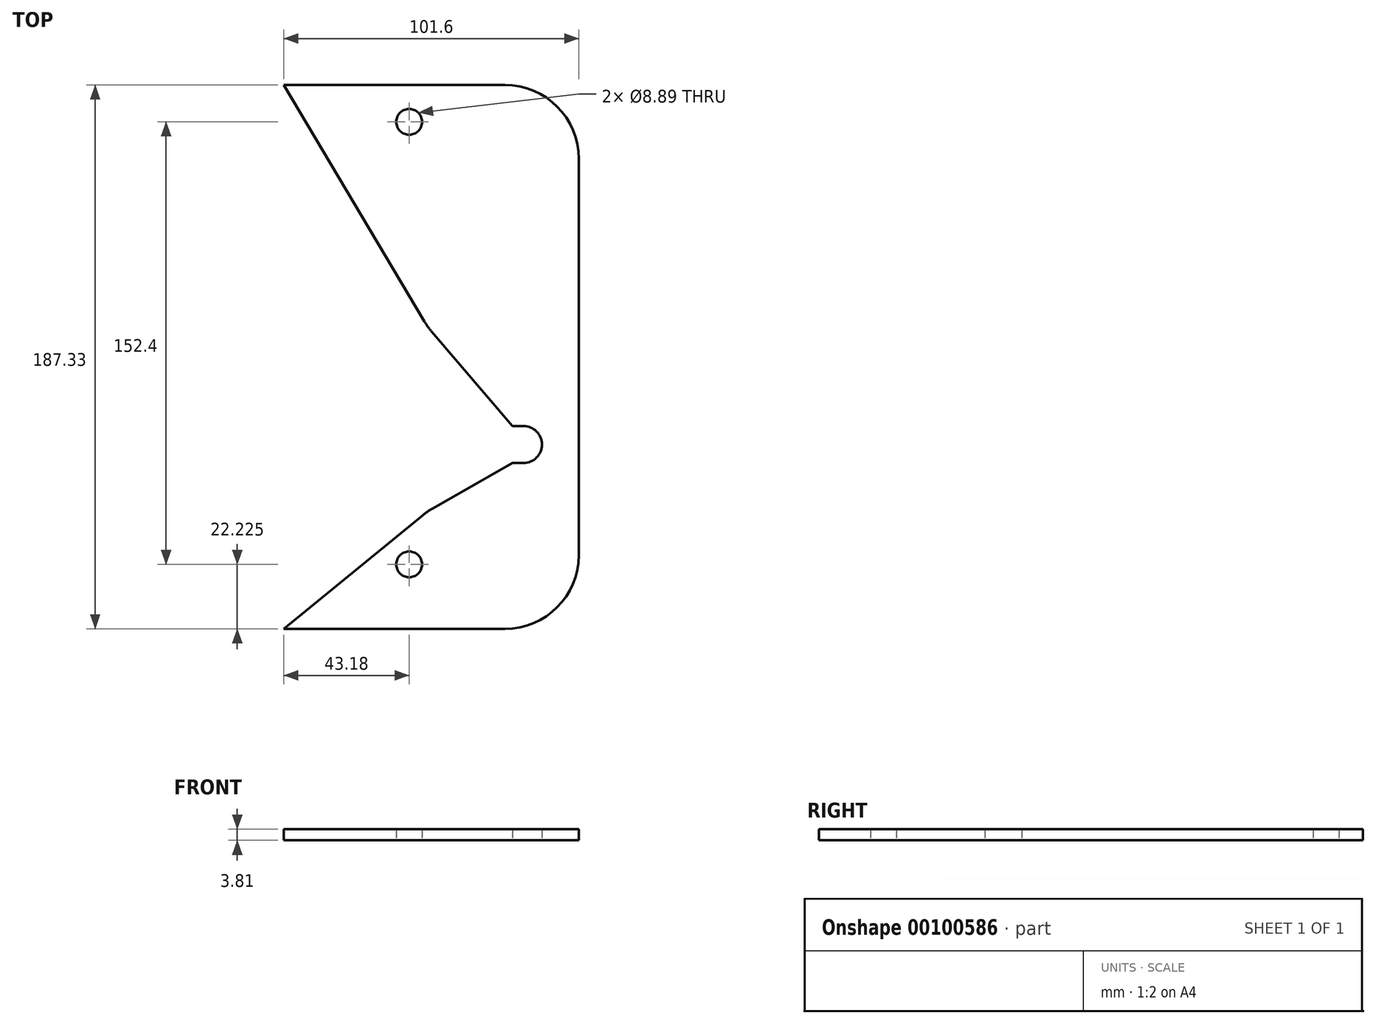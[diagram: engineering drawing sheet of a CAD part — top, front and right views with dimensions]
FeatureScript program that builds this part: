
annotation { "Feature Type Name" : "Feature", "Feature Type Description" : "" }
export const myFeature = defineFeature(function(context is Context, id is Id, definition is map)
    precondition{}
    {
        {
            var Q0;
            Q0=qCreatedBy(makeId("Top.planeOp"),FACE);
            var sketch = newSketch(context, id + "F0", { "sketchPlane" : qUnion([Q0])});
            skLineSegment(sketch, "E0.bottom", {"start": v(0, 0) * mm, "end": v(101.6, 0) * mm});
            skLineSegment(sketch, "E0.top", {"start": v(0, 187.33) * mm, "end": v(101.6, 187.33) * mm});
            skLineSegment(sketch, "E0.left", {"start": v(0, 0) * mm, "end": v(0, 187.33) * mm});
            skLineSegment(sketch, "E0.right", {"start": v(101.6, 0) * mm, "end": v(101.6, 187.33) * mm});
            skPoint(sketch, "E1.endSnap0", {"position": v(101.6, 93.66) * mm});
            skLineSegment(sketch, "E2", {"start": v(69.85, 57.15) * mm, "end": v(0, 0) * mm});
            skLineSegment(sketch, "E3", {"start": v(69.85, 69.85) * mm, "end": v(0, 187.33) * mm});
            skCircle(sketch, "E4", {"center": v(43.18, 22.23) * mm, "radius": 4.45 * mm});
            skCircle(sketch, "E5", {"center": v(43.18, 174.63) * mm, "radius": 4.45 * mm});
            skLineSegment(sketch, "E6", {"start": v(69.85, 69.85) * mm, "end": v(82.55, 69.85) * mm});
            skLineSegment(sketch, "E7", {"start": v(82.55, 69.85) * mm, "end": v(82.55, 57.15) * mm});
            skLineSegment(sketch, "E8", {"start": v(82.55, 57.15) * mm, "end": v(69.85, 57.15) * mm});
            skCircle(sketch, "E9", {"center": v(82.55, 63.5) * mm, "radius": 6.35 * mm});
            skPoint(sketch, "E10", {"position": v(88.9, 63.5) * mm});
            skLineSegment(sketch, "E11", {"start": v(78.74, 69.85) * mm, "end": v(49.53, 104.02) * mm});
            skLineSegment(sketch, "E12", {"start": v(78.74, 57.15) * mm, "end": v(49.53, 40.52) * mm});
            skSolve(sketch);
        }
        {
            var Q0;
            {var subQ5=sQuery(id+"F0.wireOp",EDGE,"E0.top");Q0=makeQuery(id+"F0.imprint","IMPRINT",FACE,{"disambiguationData":[TD([[makeQuery(id+"F0.imprint","IMPRINT",EDGE,{"derivedFrom":subQ5}),-1.0]])]});}
            var Q1;
            {var subQ6=sQuery(id+"F0.wireOp",EDGE,"E0.bottom");Q1=makeQuery(id+"F0.imprint","IMPRINT",FACE,{"disambiguationData":[TD([[makeQuery(id+"F0.imprint","IMPRINT",EDGE,{"derivedFrom":subQ6}),1.0]])]});}
            extrude(context, id + "F1", {"entities" : qUnion([Q0, Q1]), "depth" : 3.8 * mm});
        }
        {
            var Q0;
            Q0=makeQuery(id+"F1.opExtrude","SWEPT_EDGE",EDGE,{"disambiguationData":[OSD([sQuery(id+"F0.wireOp",EDGE,"E0.top"),sQuery(id+"F0.wireOp",EDGE,"E0.right")])]});
            var Q1;
            Q1=makeQuery(id+"F1.opExtrude","SWEPT_EDGE",EDGE,{"disambiguationData":[OSD([sQuery(id+"F0.wireOp",EDGE,"E0.bottom"),sQuery(id+"F0.wireOp",EDGE,"E0.right")])]});
            var Q2;
            Q2=makeQuery(id+"F1.opExtrude","SWEPT_EDGE",EDGE,{"disambiguationData":[OSD([sQuery(id+"F0.wireOp",EDGE,"E3"),sQuery(id+"F0.wireOp",EDGE,"E11")])]});
            var Q3;
            Q3=makeQuery(id+"F1.opExtrude","SWEPT_EDGE",EDGE,{"disambiguationData":[OSD([sQuery(id+"F0.wireOp",EDGE,"E2"),sQuery(id+"F0.wireOp",EDGE,"E12")])]});
            fillet(context, id + "F2", {"entities" : qUnion([Q0, Q1, Q2, Q3]), "radius" : 25.4 * mm, "tangentPropagation" : true, "allowEdgeOverflow" : false});
        }
    });
